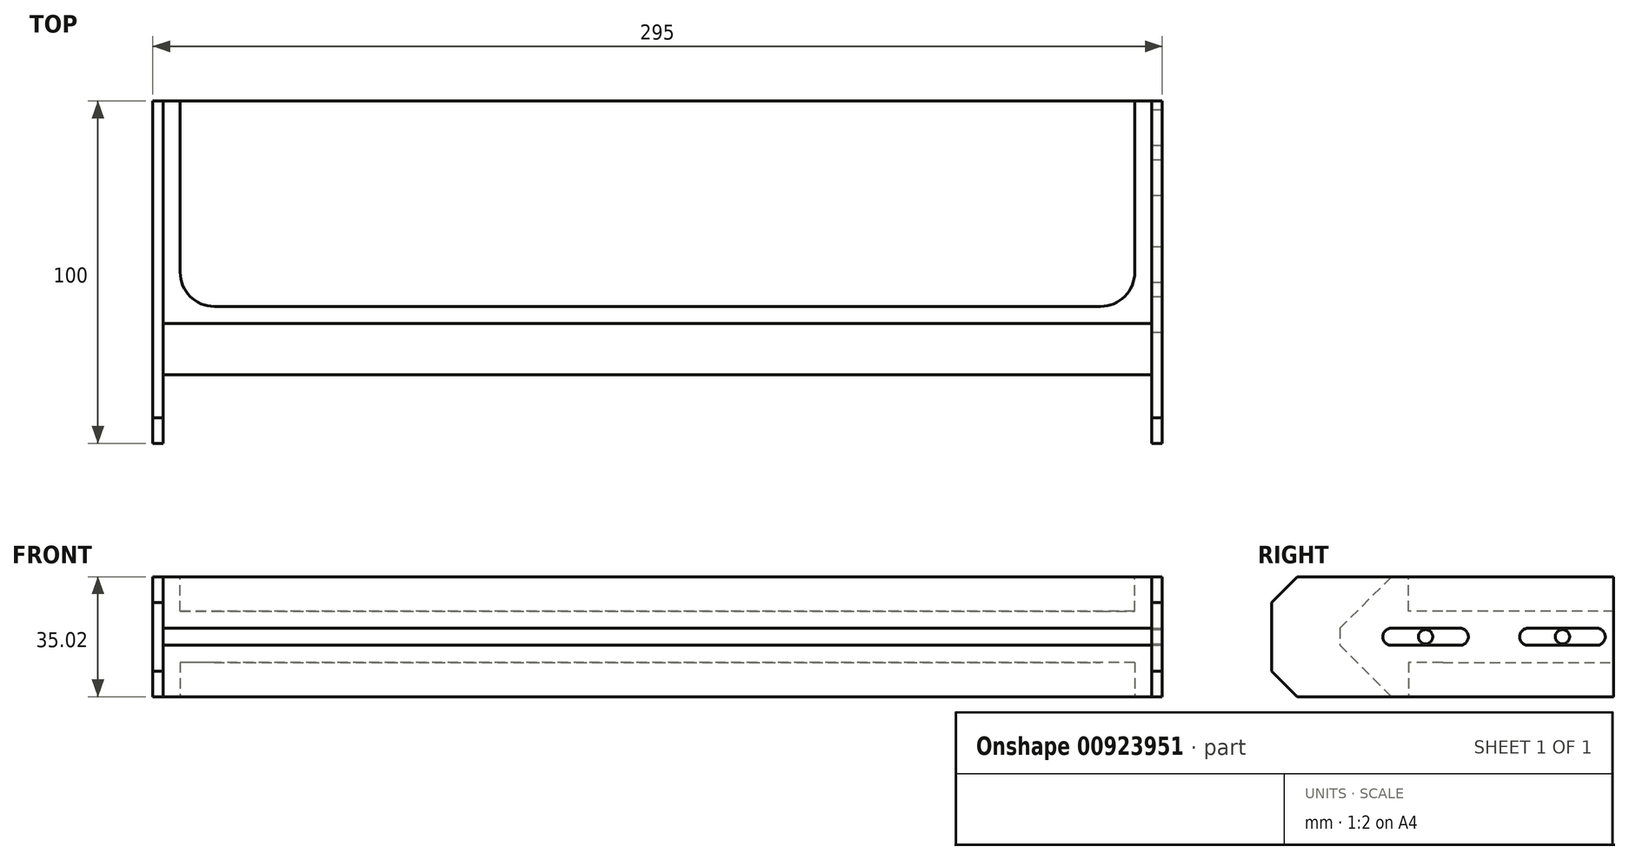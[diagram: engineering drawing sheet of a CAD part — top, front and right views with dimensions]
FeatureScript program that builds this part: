
annotation { "Feature Type Name" : "Feature", "Feature Type Description" : "" }
export const myFeature = defineFeature(function(context is Context, id is Id, definition is map)
    precondition{}
    {
        {
            var Q0;
            Q0=qCreatedBy(makeId("Top.planeOp"),FACE);
            var sketch = newSketch(context, id + "F0", { "sketchPlane" : qUnion([Q0])});
            skLineSegment(sketch, "E0.bottom", {"start": v(147.5, 50) * mm, "end": v(-147.5, 50) * mm});
            skLineSegment(sketch, "E0.top", {"start": v(147.5, -50) * mm, "end": v(144.5, -50) * mm});
            skLineSegment(sketch, "E0.left", {"start": v(147.5, 50) * mm, "end": v(147.5, -50) * mm});
            skLineSegment(sketch, "E0.right", {"start": v(-147.5, 50) * mm, "end": v(-147.5, -50) * mm});
            skPoint(sketch, "E0.middle", {"position": v(0, 0) * mm});
            skLineSegment(sketch, "E1", {"start": v(-144.5, -50) * mm, "end": v(-144.5, -30) * mm});
            skLineSegment(sketch, "E2", {"start": v(-144.5, -30) * mm, "end": v(144.5, -30) * mm});
            skLineSegment(sketch, "E3", {"start": v(144.5, -30) * mm, "end": v(144.5, -50) * mm});
            skLineSegment(sketch, "E4.trimOffspring", {"start": v(-144.5, -50) * mm, "end": v(-147.5, -50) * mm});
            skSolve(sketch);
        }
        {
            var Q0;
            Q0=qSketchRegion(id+"F0",true);
            extrude(context, id + "F1", {"entities" : qUnion([Q0]), "depth" : 17.5 * mm, "offsetDistance" : 25 * mm, "hasSecondDirection" : true, "secondDirectionOppositeDirection" : true, "secondDirectionDepth" : 17.5 * mm});
        }
        {
            var Q0;
            Q0=makeQuery(id+"F1.opExtrude","CAP_EDGE",EDGE,{"disambiguationData":[OSD([sQuery(id+"F0.wireOp",EDGE,"E2")])],"isStart":false});
            var Q1;
            Q1=makeQuery(id+"F1.opExtrude","CAP_EDGE",EDGE,{"disambiguationData":[OSD([sQuery(id+"F0.wireOp",EDGE,"E2")])],"isStart":true});
            chamfer(context, id + "F2", {"entities" : qUnion([Q0, Q1]), "width" : 15 * mm, "tangentPropagation" : true});
        }
        {
            var Q0;
            Q0=makeQuery(id+"F1.opExtrude","CAP_EDGE",EDGE,{"disambiguationData":[OSD([sQuery(id+"F0.wireOp",EDGE,"E0.top")])],"isStart":false});
            var Q1;
            Q1=makeQuery(id+"F1.opExtrude","CAP_EDGE",EDGE,{"disambiguationData":[OSD([sQuery(id+"F0.wireOp",EDGE,"E0.top")])],"isStart":true});
            var Q2;
            Q2=makeQuery(id+"F1.opExtrude","CAP_EDGE",EDGE,{"disambiguationData":[OSD([sQuery(id+"F0.wireOp",EDGE,"E4.trimOffspring")])],"isStart":false});
            var Q3;
            Q3=makeQuery(id+"F1.opExtrude","CAP_EDGE",EDGE,{"disambiguationData":[OSD([sQuery(id+"F0.wireOp",EDGE,"E4.trimOffspring")])],"isStart":true});
            chamfer(context, id + "F3", {"entities" : qUnion([Q0, Q1, Q2, Q3]), "width" : 7.5 * mm, "tangentPropagation" : true});
        }
        {
            var Q0;
            Q0=makeQuery(id+"F1.opExtrude","SWEPT_FACE",FACE,{"disambiguationData":[OSD([sQuery(id+"F0.wireOp",EDGE,"E0.left")])]});
            var sketch = newSketch(context, id + "F4", { "sketchPlane" : qUnion([Q0])});
            skLineSegment(sketch, "E5.bottom", {"start": v(45, 2.5) * mm, "end": v(25, 2.5) * mm});
            skLineSegment(sketch, "E5.top", {"start": v(45, -2.5) * mm, "end": v(25, -2.5) * mm});
            skLineSegment(sketch, "E5.left", {"start": v(47.5, 0) * mm, "end": v(47.5, 0) * mm});
            skLineSegment(sketch, "E5.right", {"start": v(22.5, 0) * mm, "end": v(22.5, 0) * mm});
            skLineSegment(sketch, "E6.bottom", {"start": v(5, 2.5) * mm, "end": v(-15, 2.5) * mm});
            skLineSegment(sketch, "E6.top", {"start": v(5, -2.5) * mm, "end": v(-15, -2.5) * mm});
            skLineSegment(sketch, "E6.left", {"start": v(7.5, 0) * mm, "end": v(7.5, 0) * mm});
            skLineSegment(sketch, "E6.right", {"start": v(-17.5, 0) * mm, "end": v(-17.5, 0) * mm});
            skPoint(sketch, "E7.visualSharp", {"position": v(-17.5, 2.5) * mm});
            skArc(sketch, "E7.filletArc", {"start": v(-15, 2.5) * mm, "mid": v(-16.77, 1.77) * mm, "end": v(-17.5, 0) * mm});
            skPoint(sketch, "E8.visualSharp", {"position": v(-17.5, -2.5) * mm});
            skArc(sketch, "E8.filletArc", {"start": v(-17.5, 0) * mm, "mid": v(-16.77, -1.77) * mm, "end": v(-15, -2.5) * mm});
            skPoint(sketch, "E9.visualSharp", {"position": v(7.5, 2.5) * mm});
            skArc(sketch, "E9.filletArc", {"start": v(7.5, 0) * mm, "mid": v(6.77, 1.77) * mm, "end": v(5, 2.5) * mm});
            skPoint(sketch, "E10.visualSharp", {"position": v(7.5, -2.5) * mm});
            skArc(sketch, "E10.filletArc", {"start": v(5, -2.5) * mm, "mid": v(6.77, -1.77) * mm, "end": v(7.5, 0) * mm});
            skPoint(sketch, "E11.visualSharp", {"position": v(22.5, 2.5) * mm});
            skArc(sketch, "E11.filletArc", {"start": v(25, 2.5) * mm, "mid": v(23.23, 1.77) * mm, "end": v(22.5, 0) * mm});
            skPoint(sketch, "E12.visualSharp", {"position": v(22.5, -2.5) * mm});
            skArc(sketch, "E12.filletArc", {"start": v(22.5, 0) * mm, "mid": v(23.23, -1.77) * mm, "end": v(25, -2.5) * mm});
            skPoint(sketch, "E13.visualSharp", {"position": v(47.5, 2.5) * mm});
            skArc(sketch, "E13.filletArc", {"start": v(47.5, 0) * mm, "mid": v(46.77, 1.77) * mm, "end": v(45, 2.5) * mm});
            skPoint(sketch, "E14.visualSharp", {"position": v(47.5, -2.5) * mm});
            skArc(sketch, "E14.filletArc", {"start": v(45, -2.5) * mm, "mid": v(46.77, -1.77) * mm, "end": v(47.5, 0) * mm});
            skCircle(sketch, "E15", {"center": v(-5, 0) * mm, "radius": 2.1 * mm});
            skCircle(sketch, "E16", {"center": v(35, 0) * mm, "radius": 2.1 * mm});
            skPoint(sketch, "E16.centerSnap0", {"position": v(35, -2.5) * mm});
            skLineSegment(sketch, "E17", {"start": v(-50, 0) * mm, "end": v(50, 0) * mm, "construction": true});
            skSolve(sketch);
        }
        {
            var Q0;
            Q0=makeQuery(id+"F1.opExtrude","CAP_FACE",FACE,{"disambiguationData":[OSD([sQuery(id+"F0.wireOp",EDGE,"E0.bottom"),sQuery(id+"F0.wireOp",EDGE,"E0.top"),sQuery(id+"F0.wireOp",EDGE,"E0.left"),sQuery(id+"F0.wireOp",EDGE,"E0.right"),sQuery(id+"F0.wireOp",EDGE,"E1"),sQuery(id+"F0.wireOp",EDGE,"E2"),sQuery(id+"F0.wireOp",EDGE,"E3"),sQuery(id+"F0.wireOp",EDGE,"E4.trimOffspring")])],"isStart":false});
            var sketch = newSketch(context, id + "F5", { "sketchPlane" : qUnion([Q0])});
            skLineSegment(sketch, "E18.bottom", {"start": v(-147.5, 50) * mm, "end": v(-144.5, 50) * mm});
            skLineSegment(sketch, "E18.top", {"start": v(-147.5, -42.5) * mm, "end": v(-144.5, -42.5) * mm});
            skLineSegment(sketch, "E18.left", {"start": v(-147.5, 50) * mm, "end": v(-147.5, -42.5) * mm});
            skLineSegment(sketch, "E18.right", {"start": v(-144.5, 50) * mm, "end": v(-144.5, -42.5) * mm});
            skLineSegment(sketch, "E19.bottom", {"start": v(147.5, 50) * mm, "end": v(144.5, 50) * mm});
            skLineSegment(sketch, "E19.top", {"start": v(147.5, -42.5) * mm, "end": v(144.5, -42.5) * mm});
            skLineSegment(sketch, "E19.left", {"start": v(147.5, 50) * mm, "end": v(147.5, -42.5) * mm});
            skLineSegment(sketch, "E19.right", {"start": v(144.5, 50) * mm, "end": v(144.5, -42.5) * mm});
            skSolve(sketch);
        }
        {
            var Q0;
            Q0=qSketchRegion(id+"F5",true);
            extrude(context, id + "F6", {"entities" : qUnion([Q0]), "operationType" : NewBodyOperationType.ADD, "depth" : 0.01 * mm, "offsetDistance" : 25 * mm});
        }
        {
            var Q0;
            Q0=makeQuery(id+"F1.opExtrude","CAP_FACE",FACE,{"disambiguationData":[OSD([sQuery(id+"F0.wireOp",EDGE,"E0.bottom"),sQuery(id+"F0.wireOp",EDGE,"E0.top"),sQuery(id+"F0.wireOp",EDGE,"E0.left"),sQuery(id+"F0.wireOp",EDGE,"E0.right"),sQuery(id+"F0.wireOp",EDGE,"E1"),sQuery(id+"F0.wireOp",EDGE,"E2"),sQuery(id+"F0.wireOp",EDGE,"E3"),sQuery(id+"F0.wireOp",EDGE,"E4.trimOffspring")])],"isStart":true});
            var sketch = newSketch(context, id + "F7", { "sketchPlane" : qUnion([Q0])});
            skLineSegment(sketch, "E20.bottom", {"start": v(-147.5, -50) * mm, "end": v(-144.5, -50) * mm});
            skLineSegment(sketch, "E20.top", {"start": v(-147.5, 42.5) * mm, "end": v(-144.5, 42.5) * mm});
            skLineSegment(sketch, "E20.left", {"start": v(-147.5, -50) * mm, "end": v(-147.5, 42.5) * mm});
            skLineSegment(sketch, "E20.right", {"start": v(-144.5, -50) * mm, "end": v(-144.5, 42.5) * mm});
            skLineSegment(sketch, "E21.bottom", {"start": v(147.5, -50) * mm, "end": v(144.5, -50) * mm});
            skLineSegment(sketch, "E21.top", {"start": v(147.5, 42.5) * mm, "end": v(144.5, 42.5) * mm});
            skLineSegment(sketch, "E21.left", {"start": v(147.5, -50) * mm, "end": v(147.5, 42.5) * mm});
            skLineSegment(sketch, "E21.right", {"start": v(144.5, -50) * mm, "end": v(144.5, 42.5) * mm});
            skSolve(sketch);
        }
        {
            var Q0;
            Q0=qSketchRegion(id+"F7",true);
            extrude(context, id + "F8", {"entities" : qUnion([Q0]), "operationType" : NewBodyOperationType.ADD, "depth" : 0.01 * mm, "offsetDistance" : 25 * mm});
        }
        {
            var Q0;
            Q0=makeQuery(id+"F4.imprint","IMPRINT",FACE,{"disambiguationData":[TD([[makeQuery(id+"F4.imprint","IMPRINT",EDGE,{"derivedFrom":sQuery(id+"F4.wireOp",EDGE,"E5.bottom")}),1.0]])]});
            var Q1;
            Q1=makeQuery(id+"F4.imprint","IMPRINT",FACE,{"disambiguationData":[TD([[makeQuery(id+"F4.imprint","IMPRINT",EDGE,{"derivedFrom":sQuery(id+"F4.wireOp",EDGE,"E6.bottom")}),1.0]])]});
            extrude(context, id + "F9", {"entities" : qUnion([Q0, Q1]), "operationType" : NewBodyOperationType.REMOVE, "oppositeDirection" : true, "depth" : 3 * mm, "offsetDistance" : 25 * mm});
        }
        {
            var Q0;
            Q0=makeQuery(id+"F1.opExtrude","CAP_FACE",FACE,{"disambiguationData":[OSD([sQuery(id+"F0.wireOp",EDGE,"E0.bottom"),sQuery(id+"F0.wireOp",EDGE,"E0.top"),sQuery(id+"F0.wireOp",EDGE,"E0.left"),sQuery(id+"F0.wireOp",EDGE,"E0.right"),sQuery(id+"F0.wireOp",EDGE,"E1"),sQuery(id+"F0.wireOp",EDGE,"E2"),sQuery(id+"F0.wireOp",EDGE,"E3"),sQuery(id+"F0.wireOp",EDGE,"E4.trimOffspring")])],"isStart":false});
            var sketch = newSketch(context, id + "F10", { "sketchPlane" : qUnion([Q0])});
            skLineSegment(sketch, "E22.bottom", {"start": v(-139.5, 50) * mm, "end": v(139.5, 50) * mm});
            skLineSegment(sketch, "E22.top", {"start": v(-129.5, -10) * mm, "end": v(129.5, -10) * mm});
            skLineSegment(sketch, "E22.left", {"start": v(-139.5, 50) * mm, "end": v(-139.5, 0) * mm});
            skLineSegment(sketch, "E22.right", {"start": v(139.5, 50) * mm, "end": v(139.5, 0) * mm});
            skPoint(sketch, "E23.visualSharp", {"position": v(-139.5, -10) * mm});
            skArc(sketch, "E23.filletArc", {"start": v(-139.5, 0) * mm, "mid": v(-136.57, -7.07) * mm, "end": v(-129.5, -10) * mm});
            skPoint(sketch, "E24.visualSharp", {"position": v(139.5, -10) * mm});
            skArc(sketch, "E24.filletArc", {"start": v(129.5, -10) * mm, "mid": v(136.57, -7.07) * mm, "end": v(139.5, 0) * mm});
            skSolve(sketch);
        }
        {
            var Q0;
            Q0=makeQuery(id+"F10.imprint","IMPRINT",FACE,{"disambiguationData":[TD([[makeQuery(id+"F10.imprint","IMPRINT",EDGE,{"derivedFrom":sQuery(id+"F10.wireOp",EDGE,"E22.bottom")}),1.0]])]});
            extrude(context, id + "F11", {"entities" : qUnion([Q0]), "operationType" : NewBodyOperationType.REMOVE, "oppositeDirection" : true, "depth" : 10 * mm, "offsetDistance" : 25 * mm});
        }
        {
            var Q0;
            Q0=makeQuery(id+"F1.opExtrude","CAP_FACE",FACE,{"disambiguationData":[OSD([sQuery(id+"F0.wireOp",EDGE,"E0.bottom"),sQuery(id+"F0.wireOp",EDGE,"E0.top"),sQuery(id+"F0.wireOp",EDGE,"E0.left"),sQuery(id+"F0.wireOp",EDGE,"E0.right"),sQuery(id+"F0.wireOp",EDGE,"E1"),sQuery(id+"F0.wireOp",EDGE,"E2"),sQuery(id+"F0.wireOp",EDGE,"E3"),sQuery(id+"F0.wireOp",EDGE,"E4.trimOffspring")])],"isStart":true});
            var sketch = newSketch(context, id + "F12", { "sketchPlane" : qUnion([Q0])});
            skLineSegment(sketch, "E25.0.0", {"start": v(139.5, 0) * mm, "end": v(139.5, -50) * mm});
            skLineSegment(sketch, "E25.0.1", {"start": v(139.5, -50) * mm, "end": v(-139.5, -50) * mm});
            skLineSegment(sketch, "E25.0.2", {"start": v(-139.5, -50) * mm, "end": v(-139.5, 0) * mm});
            skArc(sketch, "E25.0.3", {"start": v(-139.5, 0) * mm, "mid": v(-136.57, 7.07) * mm, "end": v(-129.5, 10) * mm});
            skLineSegment(sketch, "E25.0.4", {"start": v(-129.5, 10) * mm, "end": v(129.5, 10) * mm});
            skArc(sketch, "E25.0.5", {"start": v(129.5, 10) * mm, "mid": v(136.57, 7.07) * mm, "end": v(139.5, 0) * mm});
            skSolve(sketch);
        }
        {
            var Q0;
            Q0=qSketchRegion(id+"F12",true);
            extrude(context, id + "F13", {"entities" : qUnion([Q0]), "operationType" : NewBodyOperationType.REMOVE, "oppositeDirection" : true, "depth" : 10 * mm, "offsetDistance" : 25 * mm});
        }
    });
